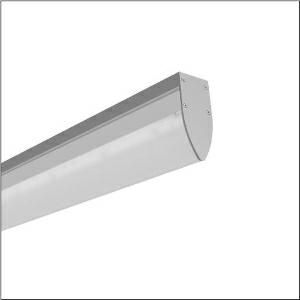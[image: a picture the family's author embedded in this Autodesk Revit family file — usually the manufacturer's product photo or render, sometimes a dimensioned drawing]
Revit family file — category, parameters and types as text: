
# Revit family: mira_21_td_51fr527d424a
name_source: partatom
category: Lighting Fixtures
units: mm (PartAtom-declared; Revit-internal decimal feet)

## family parameters
Cut with Voids When Loaded = No
Host = Face
Light Source = No
Part Type = Normal
Room Calculation Point = No
Round Connector Dimension = Use Diameter
Shared = No

## types (1)
- Mira 21 TD (1 x LED, 2020 lm, 14 W, 4000K)
    Apparent Load = 14 VA
    CIE Flux Codes = 40 68 87 81 100
    Color Rendering = 80
    Color Temperature = 4000K
    Default Elevation = 1800 mm
    Description = Mira 21 TD, clean room luminaire, primary light control with reflector, primary optical cover: cover, of PMMA, frosted, light emission: direct distribution, primary light characteristic: symmetric, installation type: surface-mounted, LED, rated luminous flux: 2.020lm, luminous efficacy: 144lm/W, light colour: 840, colour temperature: 4000K, control gear: ON/OFF, with terminal, 3-pole, max. 2.5mm², mains connection: 230V, AC, 50/60Hz, rated input power: 14W, luminaire housing, of sheet steel, coated, pure white (RAL 9010), length: 600mm, width: 55mm, height: 120mm, protection rating (complete): IP43, insulation class (complete): insulation class I (protective earthing), certification: CE, UKCA, permissible operating ambient temperature: -5..+40°C, standard: EN 50419, packaging unit: 1 piece
    Height = 120 mm
    Lamp = 1 x LED
    Lamp Light Flux = 2020 lm
    Lamp Power = 14 W
    Lamp count = 1
    Length = 600 mm
    Luminous efficacy = 144 lm/W
    Manufacturer = Siteco
    ModVariant = No
    Model = 51FR527D424A
    Mounting Place = Ceiling
    Mounting Type = Surface mounted
    Number of Poles = 1
    OnlyDefault = Yes
    Power Factor = 1
    Product Name = Mira 21 TD
    Product group = clean room luminaire | ceiling mounted
    ProductGroupID = 306
    Protection Class = Protection class I
    Protection Degree = IP 43
    RLX_Detail_Level = 1
    RLX_Emergency_Light_Flux = 0 lm
    RLX_Emergency_Type = 0
    RLX_Emergency_Type_DB = No
    RlxData = <blob elided: 25913 chars, md5=bd9307f1>
    Socket = socket
    Standby Power = 0 W
    System Light Flux = 2020 lm
    System Power = 14 W
    Type Comments = Product without accessories
    Type Image = l_1007115.jpg
    URL = http://relux.com
    VarID = ---
    Voltage = 0 V
    Weight = 0.00 kg
    Width = 55 mm

## geometry (parser evidence)
native form markers: Blend x4, Sweep x14
no freeform markers — native parametric forms only
